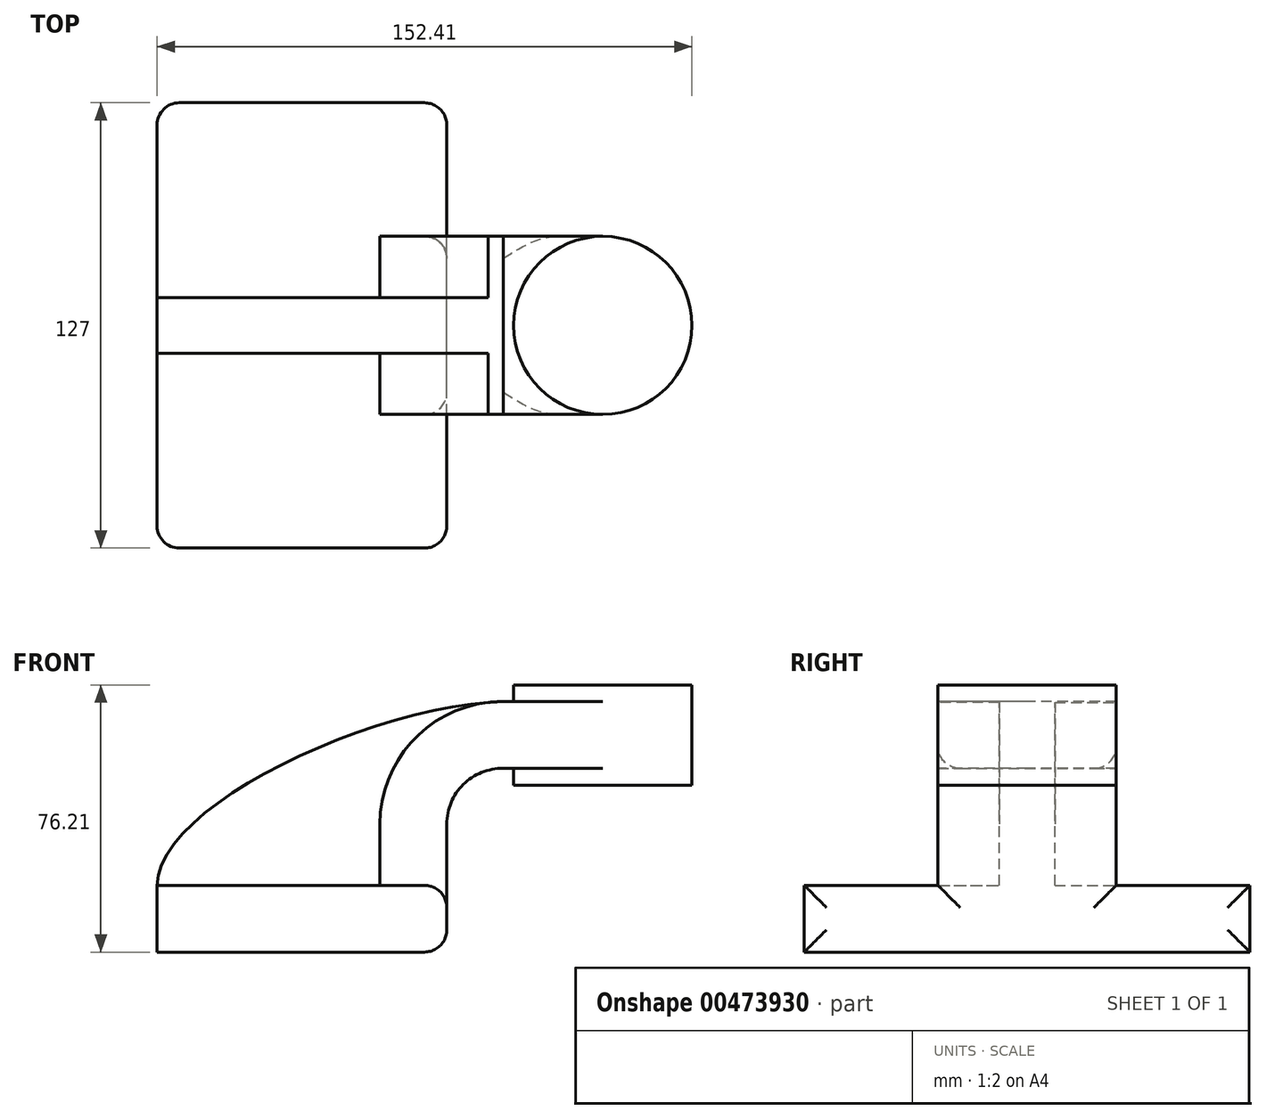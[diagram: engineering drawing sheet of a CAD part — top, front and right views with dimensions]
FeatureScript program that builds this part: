
annotation { "Feature Type Name" : "Feature", "Feature Type Description" : "" }
export const myFeature = defineFeature(function(context is Context, id is Id, definition is map)
    precondition{}
    {
        {
            var Q0;
            Q0=qCreatedBy(makeId("Front.planeOp"),FACE);
            var sketch = newSketch(context, id + "F0", { "sketchPlane" : qUnion([Q0])});
            skLineSegment(sketch, "E0.bottom", {"start": v(41.28, -9.52) * mm, "end": v(-41.28, -9.53) * mm});
            skLineSegment(sketch, "E0.top", {"start": v(41.28, 9.53) * mm, "end": v(-41.28, 9.53) * mm});
            skLineSegment(sketch, "E0.left", {"start": v(41.28, -9.52) * mm, "end": v(41.28, 9.53) * mm});
            skLineSegment(sketch, "E0.right", {"start": v(-41.28, -9.53) * mm, "end": v(-41.28, 9.53) * mm});
            skPoint(sketch, "E0.middle", {"position": v(0, 0) * mm});
            skLineSegment(sketch, "E1.bottom", {"start": v(111.12, 38.1) * mm, "end": v(60.33, 38.1) * mm});
            skLineSegment(sketch, "E1.top", {"start": v(111.12, 66.68) * mm, "end": v(60.33, 66.68) * mm});
            skLineSegment(sketch, "E1.left", {"start": v(111.12, 38.1) * mm, "end": v(111.12, 66.68) * mm});
            skLineSegment(sketch, "E1.right", {"start": v(60.33, 38.1) * mm, "end": v(60.33, 66.68) * mm});
            skPoint(sketch, "E1.middle", {"position": v(85.72, 52.39) * mm});
            skLineSegment(sketch, "E2", {"start": v(41.28, 9.53) * mm, "end": v(41.28, 27) * mm});
            skArc(sketch, "E3", {"start": v(41.27, 27) * mm, "mid": v(45.97, 38.27) * mm, "end": v(57.28, 42.88) * mm});
            skLineSegment(sketch, "E4", {"start": v(57.28, 42.88) * mm, "end": v(85.72, 42.88) * mm});
            skPoint(sketch, "E4.endSnap0", {"position": v(85.72, 38.1) * mm});
            skLineSegment(sketch, "E5.0", {"start": v(57.34, 61.93) * mm, "end": v(85.72, 61.93) * mm});
            skArc(sketch, "E5.1", {"start": v(22.23, 27) * mm, "mid": v(32.52, 51.76) * mm, "end": v(57.34, 61.93) * mm});
            skLineSegment(sketch, "E5.2", {"start": v(22.22, 9.53) * mm, "end": v(22.22, 27) * mm});
            skLineSegment(sketch, "E6", {"start": v(85.72, 38.1) * mm, "end": v(85.72, 66.68) * mm});
            skFitSpline(sketch, "E7", {"points": [v(-41.28, 9.53) * mm, v(57.34, 61.93) * mm], "startDerivative": vector(0, 67.83) * mm, "endDerivative": vector(112.54, 3.42) * mm});
            skSolve(sketch);
        }
        {
            var Q0;
            Q0=makeQuery(id+"F0.imprint","IMPRINT",FACE,{"disambiguationData":[TD([[makeQuery(id+"F0.imprint","IMPRINT",EDGE,{"derivedFrom":sQuery(id+"F0.wireOp",EDGE,"E0.bottom")}),-1.0]])]});
            extrude(context, id + "F1", {"entities" : qUnion([Q0]), "endBound" : BoundingType.SYMMETRIC, "depth" : 127 * mm});
        }
        {
            var Q0;
            {var subQ1=sQuery(id+"F0.wireOp",EDGE,"E2");Q0=makeQuery(id+"F0.imprint","IMPRINT",FACE,{"disambiguationData":[TD([[makeQuery(id+"F0.imprint","IMPRINT",EDGE,{"derivedFrom":subQ1}),1.0]])]});}
            var Q1;
            {var subQ0=sQuery(id+"F0.wireOp",EDGE,"E4");var subQ1=sQuery(id+"F0.wireOp",EDGE,"E1.right");var subQ2=makeQuery(id+"F0.imprint","INTERSECT",VERTEX,{"derivedFrom":[subQ1,subQ0]});Q1=makeQuery(id+"F0.imprint","IMPRINT",FACE,{"disambiguationData":[TD([[makeQuery(id+"F0.imprint","IMPRINT",EDGE,{"disambiguationData":[TD([[subQ2,-1.0]])],"derivedFrom":subQ1}),-1.0]])]});}
            extrude(context, id + "F2", {"entities" : qUnion([Q0, Q1]), "operationType" : NewBodyOperationType.ADD, "endBound" : BoundingType.SYMMETRIC, "depth" : 50.8 * mm});
        }
        {
            var Q0;
            {var subQ3=sQuery(id+"F0.wireOp",EDGE,"E5.2");Q0=makeQuery(id+"F0.imprint","IMPRINT",FACE,{"disambiguationData":[TD([[makeQuery(id+"F0.imprint","IMPRINT",EDGE,{"derivedFrom":subQ3}),1.0]])]});}
            extrude(context, id + "F3", {"entities" : qUnion([Q0]), "operationType" : NewBodyOperationType.ADD, "endBound" : BoundingType.SYMMETRIC, "depth" : 15.88 * mm});
        }
        {
            var Q0;
            {var subQ0=sQuery(id+"F0.wireOp",EDGE,"E1.left");Q0=makeQuery(id+"F0.imprint","IMPRINT",FACE,{"disambiguationData":[TD([[makeQuery(id+"F0.imprint","IMPRINT",EDGE,{"derivedFrom":subQ0}),1.0]])]});}
            var Q1;
            Q1=sQuery(id+"F0.wireOp",EDGE,"E6");
            revolve(context, id + "F4", {"operationType" : NewBodyOperationType.ADD, "entities" : qUnion([Q0]), "axis" : qUnion([Q1]), "revolveType" : RevolveType.FULL});
        }
        {
            var Q0;
            Q0=makeQuery(id+"F1.opExtrude","CAP_EDGE",EDGE,{"disambiguationData":[OSD([sQuery(id+"F0.wireOp",EDGE,"E0.left")])],"isStart":false});
            var Q1;
            Q1=makeQuery(id+"F1.opExtrude","CAP_EDGE",EDGE,{"disambiguationData":[OSD([sQuery(id+"F0.wireOp",EDGE,"E0.right")])],"isStart":false});
            var Q2;
            Q2=makeQuery(id+"F2.boolean.opBoolean","MERGE",FACE,{"derivedFrom":[makeQuery(id+"F1.opExtrude","SWEPT_FACE",FACE,{"disambiguationData":[OSD([sQuery(id+"F0.wireOp",EDGE,"E0.left")])]}),makeQuery(id+"F2.opExtrude","SWEPT_FACE",FACE,{"disambiguationData":[OSD([sQuery(id+"F0.wireOp",EDGE,"E2")])]})]});
            var Q3;
            Q3=makeQuery(id+"F1.opExtrude","CAP_EDGE",EDGE,{"disambiguationData":[OSD([sQuery(id+"F0.wireOp",EDGE,"E0.right")])],"isStart":true});
            fillet(context, id + "F5", {"entities" : qUnion([Q0, Q1, Q2, Q3]), "radius" : 6.35 * mm, "tangentPropagation" : true, "allowEdgeOverflow" : false});
        }
    });
